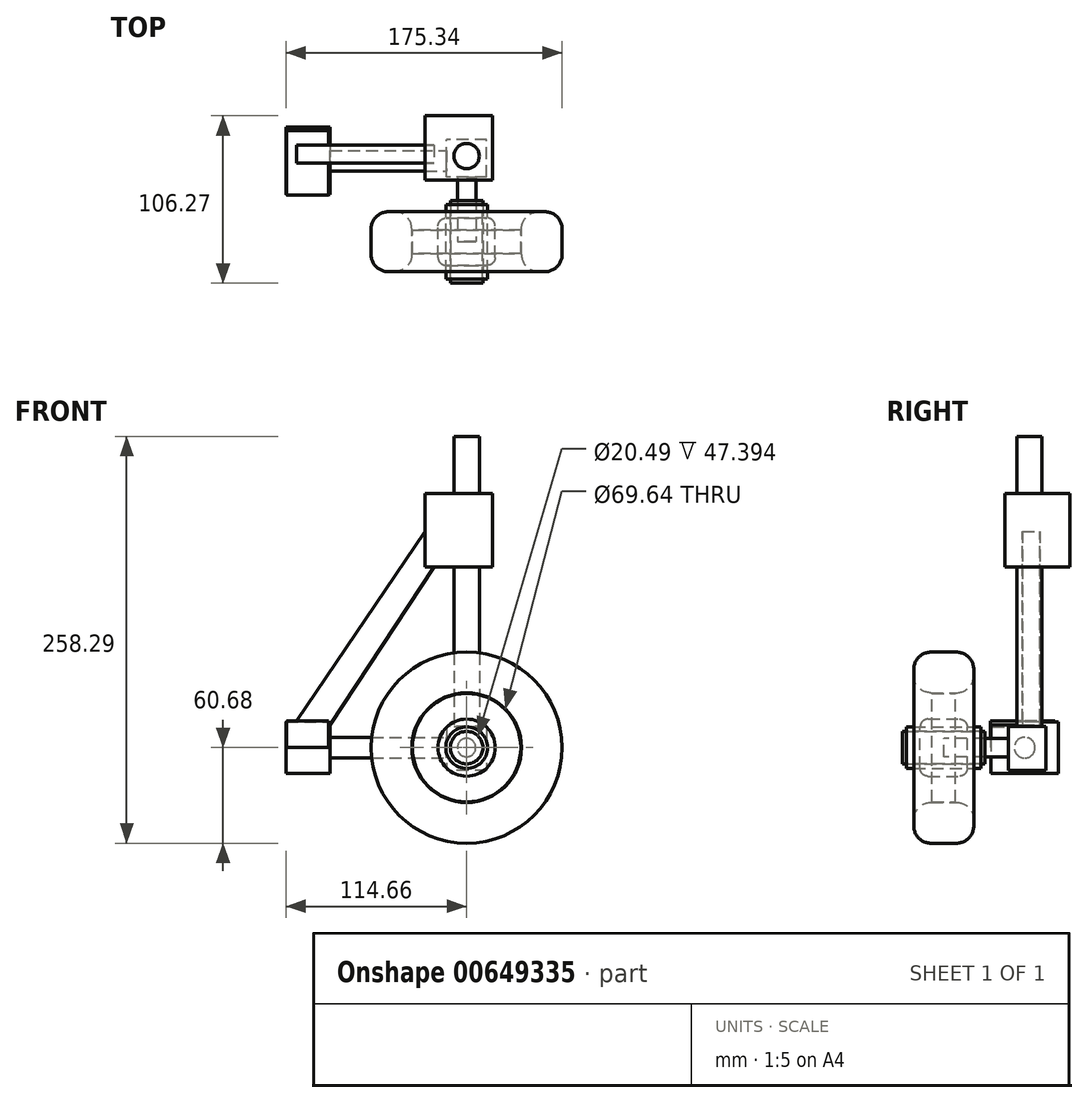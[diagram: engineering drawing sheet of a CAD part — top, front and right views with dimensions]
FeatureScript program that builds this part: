
annotation { "Feature Type Name" : "Feature", "Feature Type Description" : "" }
export const myFeature = defineFeature(function(context is Context, id is Id, definition is map)
    precondition{}
    {
        {
            var Q0;
            Q0=qCreatedBy(makeId("Front.planeOp"),FACE);
            var sketch = newSketch(context, id + "F0", { "sketchPlane" : qUnion([Q0])});
            skCircle(sketch, "E0", {"center": v(0, 0) * mm, "radius": 34.82 * mm});
            skCircle(sketch, "E1", {"center": v(0, 0) * mm, "radius": 60.68 * mm});
            skSolve(sketch);
        }
        {
            var Q0;
            Q0=makeQuery(id+"F0.imprint","IMPRINT",FACE,{"disambiguationData":[TD([[makeQuery(id+"F0.imprint","IMPRINT",EDGE,{"derivedFrom":sQuery(id+"F0.wireOp",EDGE,"E0")}),-1.0]])]});
            extrude(context, id + "F1", {"entities" : qUnion([Q0]), "endBound" : BoundingType.SYMMETRIC, "depth" : 38.1 * mm, "offsetDistance" : 25.4 * mm});
        }
        {
            var Q0;
            Q0=qCreatedBy(makeId("Front.planeOp"),FACE);
            var sketch = newSketch(context, id + "F2", { "sketchPlane" : qUnion([Q0])});
            skCircle(sketch, "E2", {"center": v(0, 0) * mm, "radius": 34.45 * mm});
            skSolve(sketch);
        }
        {
            var Q0;
            Q0 = qSketchRegion(id + "F2", true);
            extrude(context, id + "F3", {"entities" : qUnion([Q0]), "endBound" : BoundingType.SYMMETRIC, "depth" : 14.73 * mm, "offsetDistance" : 25.4 * mm});
        }
        {
            var Q0;
            Q0=makeQuery(id+"F1.opExtrude","CAP_EDGE",EDGE,{"disambiguationData":[OSD([sQuery(id+"F0.wireOp",EDGE,"E1")])],"isStart":true});
            var Q1;
            Q1=makeQuery(id+"F1.opExtrude","CAP_EDGE",EDGE,{"disambiguationData":[OSD([sQuery(id+"F0.wireOp",EDGE,"E0")])],"isStart":true});
            var Q2;
            Q2=makeQuery(id+"F1.opExtrude","CAP_EDGE",EDGE,{"disambiguationData":[OSD([sQuery(id+"F0.wireOp",EDGE,"E1")])],"isStart":false});
            var Q3;
            Q3=makeQuery(id+"F1.opExtrude","CAP_EDGE",EDGE,{"disambiguationData":[OSD([sQuery(id+"F0.wireOp",EDGE,"E0")])],"isStart":false});
            fillet(context, id + "F4", {"entities" : qUnion([Q0, Q1, Q2, Q3]), "radius" : 11.04 * mm, "tangentPropagation" : true, "allowEdgeOverflow" : false});
        }
        {
            var Q0;
            Q0=qCreatedBy(makeId("Front.planeOp"),FACE);
            var sketch = newSketch(context, id + "F5", { "sketchPlane" : qUnion([Q0])});
            skCircle(sketch, "E3", {"center": v(0, 0) * mm, "radius": 18.16 * mm});
            skSolve(sketch);
        }
        {
            var Q0;
            Q0 = qSketchRegion(id + "F5", true);
            extrude(context, id + "F6", {"entities" : qUnion([Q0]), "endBound" : BoundingType.SYMMETRIC, "depth" : 29.97 * mm, "offsetDistance" : 25.4 * mm});
        }
        {
            var Q0;
            Q0=makeQuery(id+"F6.opExtrude","CAP_EDGE",EDGE,{"disambiguationData":[OSD([sQuery(id+"F5.wireOp",EDGE,"E3")])],"isStart":false});
            var Q1;
            Q1=makeQuery(id+"F6.opExtrude","CAP_FACE",FACE,{"disambiguationData":[OSD([sQuery(id+"F5.wireOp",EDGE,"E3")])],"isStart":true});
            fillet(context, id + "F7", {"entities" : qUnion([Q0, Q1]), "radius" : 5.08 * mm, "tangentPropagation" : true, "allowEdgeOverflow" : false});
        }
        {
            var Q0;
            Q0=qCreatedBy(makeId("Front.planeOp"),FACE);
            var sketch = newSketch(context, id + "F8", { "sketchPlane" : qUnion([Q0])});
            skCircle(sketch, "E4", {"center": v(0, 0) * mm, "radius": 13.2 * mm});
            skCircle(sketch, "E5", {"center": v(0, 0) * mm, "radius": 10.25 * mm});
            skSolve(sketch);
        }
        {
            var Q0;
            Q0 = qSketchRegion(id + "F8", true);
            extrude(context, id + "F9", {"entities" : qUnion([Q0]), "endBound" : BoundingType.SYMMETRIC, "depth" : 47.4 * mm, "offsetDistance" : 25.4 * mm});
        }
        {
            var Q0;
            Q0=qCreatedBy(makeId("Front.planeOp"),FACE);
            var sketch = newSketch(context, id + "F10", { "sketchPlane" : qUnion([Q0])});
            skCircle(sketch, "E6", {"center": v(0, 0) * mm, "radius": 10.34 * mm});
            skSolve(sketch);
        }
        {
            var Q0;
            Q0 = qSketchRegion(id + "F10", true);
            extrude(context, id + "F11", {"entities" : qUnion([Q0]), "endBound" : BoundingType.SYMMETRIC, "oppositeDirection" : true, "depth" : 52.48 * mm, "offsetDistance" : 25.4 * mm});
        }
        {
            var Q0;
            Q0=qCreatedBy(makeId("Front.planeOp"),FACE);
            var sketch = newSketch(context, id + "F12", { "sketchPlane" : qUnion([Q0])});
            skCircle(sketch, "E7", {"center": v(0, 0) * mm, "radius": 5.84 * mm});
            skSolve(sketch);
        }
        {
            var Q0;
            Q0 = qSketchRegion(id + "F12", true);
            extrude(context, id + "F13", {"entities" : qUnion([Q0]), "oppositeDirection" : true, "depth" : 50.72 * mm, "offsetDistance" : 25.4 * mm});
        }
        {
            var Q0;
            Q0=qCreatedBy(makeId("Right.planeOp"),FACE);
            var sketch = newSketch(context, id + "F14", { "sketchPlane" : qUnion([Q0])});
            skLineSegment(sketch, "E8.bottom", {"start": v(41.05, 13.44) * mm, "end": v(64.93, 13.44) * mm});
            skLineSegment(sketch, "E8.top", {"start": v(41.05, -14.38) * mm, "end": v(64.93, -14.38) * mm});
            skLineSegment(sketch, "E8.left", {"start": v(41.05, 13.44) * mm, "end": v(41.05, -14.38) * mm});
            skLineSegment(sketch, "E8.right", {"start": v(64.93, 13.44) * mm, "end": v(64.93, -14.38) * mm});
            skSolve(sketch);
        }
        {
            var Q0;
            Q0 = qSketchRegion(id + "F14", true);
            extrude(context, id + "F15", {"entities" : qUnion([Q0]), "operationType" : NewBodyOperationType.ADD, "endBound" : BoundingType.SYMMETRIC, "depth" : 25.4 * mm, "offsetDistance" : 25.4 * mm});
        }
        {
            var Q0;
            Q0=qCreatedBy(makeId("Top.planeOp"),FACE);
            var sketch = newSketch(context, id + "F16", { "sketchPlane" : qUnion([Q0])});
            skCircle(sketch, "E9", {"center": v(0, 54.42) * mm, "radius": 8.07 * mm});
            skSolve(sketch);
        }
        {
            var Q0;
            Q0 = qSketchRegion(id + "F16", true);
            extrude(context, id + "F17", {"entities" : qUnion([Q0]), "operationType" : NewBodyOperationType.ADD, "depth" : 197.61 * mm, "offsetDistance" : 25.4 * mm});
        }
        {
            var Q0;
            Q0=qCreatedBy(makeId("Right.planeOp"),FACE);
            var sketch = newSketch(context, id + "F18", { "sketchPlane" : qUnion([Q0])});
            skCircle(sketch, "E10", {"center": v(51.45, 0) * mm, "radius": 6.59 * mm});
            skSolve(sketch);
        }
        {
            var Q0;
            Q0 = qSketchRegion(id + "F18", true);
            extrude(context, id + "F19", {"entities" : qUnion([Q0]), "operationType" : NewBodyOperationType.ADD, "oppositeDirection" : true, "depth" : 106.85 * mm, "offsetDistance" : 25.4 * mm});
        }
        {
            var Q0;
            Q0=qCreatedBy(makeId("Front.planeOp"),FACE);
            var sketch = newSketch(context, id + "F20", { "sketchPlane" : qUnion([Q0])});
            skLineSegment(sketch, "E11.bottom", {"start": v(-86.73, 16.5) * mm, "end": v(-114.66, 16.5) * mm});
            skLineSegment(sketch, "E11.top", {"start": v(-86.73, -16.5) * mm, "end": v(-114.66, -16.5) * mm});
            skLineSegment(sketch, "E11.left", {"start": v(-86.73, 16.5) * mm, "end": v(-86.73, -16.5) * mm});
            skLineSegment(sketch, "E11.right", {"start": v(-114.66, 16.5) * mm, "end": v(-114.66, -16.5) * mm});
            skPoint(sketch, "E11.middle", {"position": v(-100.7, 0) * mm});
            skSolve(sketch);
        }
        {
            var Q0;
            Q0=makeQuery(id+"F20.imprint","IMPRINT",FACE,{"disambiguationData":[TD([[makeQuery(id+"F20.imprint","IMPRINT",EDGE,{"derivedFrom":sQuery(id+"F20.wireOp",EDGE,"E11.bottom")}),1.0]])]});
            extrude(context, id + "F21", {"entities" : qUnion([Q0]), "operationType" : NewBodyOperationType.ADD, "oppositeDirection" : true, "depth" : 72.76 * mm, "offsetDistance" : 25.4 * mm});
        }
        {
            var Q0;
            Q0=makeQuery(id+"F21.opExtrude","CAP_FACE",FACE,{"disambiguationData":[OSD([sQuery(id+"F20.wireOp",EDGE,"E11.bottom"),sQuery(id+"F20.wireOp",EDGE,"E11.top"),sQuery(id+"F20.wireOp",EDGE,"E11.left"),sQuery(id+"F20.wireOp",EDGE,"E11.right")])],"isStart":true});
            extrude(context, id + "F22", {"entities" : qUnion([Q0]), "operationType" : NewBodyOperationType.REMOVE, "oppositeDirection" : true, "depth" : 30.1 * mm, "offsetDistance" : 25.4 * mm});
        }
        {
            var Q0;
            Q0=qCreatedBy(makeId("Front.planeOp"),FACE);
            var sketch = newSketch(context, id + "F23", { "sketchPlane" : qUnion([Q0])});
            skLineSegment(sketch, "E12", {"start": v(-109.7, 14.62) * mm, "end": v(-13.9, 155.72) * mm});
            skLineSegment(sketch, "E13", {"start": v(-13.9, 155.72) * mm, "end": v(0, 146.29) * mm});
            skLineSegment(sketch, "E14", {"start": v(0, 146.29) * mm, "end": v(-96.22, 0) * mm});
            skLineSegment(sketch, "E15", {"start": v(-96.22, 0) * mm, "end": v(-109.7, 14.62) * mm});
            skSolve(sketch);
        }
        {
            var Q0;
            Q0=makeQuery(id+"F23.imprint","IMPRINT",FACE,{"disambiguationData":[TD([[makeQuery(id+"F23.imprint","IMPRINT",EDGE,{"derivedFrom":sQuery(id+"F23.wireOp",EDGE,"E12")}),-1.0]])]});
            extrude(context, id + "F24", {"entities" : qUnion([Q0]), "operationType" : NewBodyOperationType.ADD, "oppositeDirection" : true, "depth" : 61.23 * mm, "offsetDistance" : 25.4 * mm});
        }
        {
            var Q0;
            Q0=makeQuery(id+"F24.opExtrude","CAP_FACE",FACE,{"disambiguationData":[OSD([sQuery(id+"F23.wireOp",EDGE,"E12"),sQuery(id+"F23.wireOp",EDGE,"E13"),sQuery(id+"F23.wireOp",EDGE,"E14"),sQuery(id+"F23.wireOp",EDGE,"E15")])],"isStart":true});
            extrude(context, id + "F25", {"entities" : qUnion([Q0]), "operationType" : NewBodyOperationType.REMOVE, "oppositeDirection" : true, "depth" : 50.06 * mm, "offsetDistance" : 25.4 * mm});
        }
        {
            var Q0;
            Q0=qCreatedBy(makeId("Front.planeOp"),FACE);
            var sketch = newSketch(context, id + "F26", { "sketchPlane" : qUnion([Q0])});
            skLineSegment(sketch, "E16.bottom", {"start": v(-26.38, 161.4) * mm, "end": v(16.55, 161.4) * mm});
            skLineSegment(sketch, "E16.top", {"start": v(-26.38, 114.78) * mm, "end": v(16.55, 114.78) * mm});
            skLineSegment(sketch, "E16.left", {"start": v(-26.38, 161.4) * mm, "end": v(-26.38, 114.78) * mm});
            skLineSegment(sketch, "E16.right", {"start": v(16.55, 161.4) * mm, "end": v(16.55, 114.78) * mm});
            skSolve(sketch);
        }
        {
            var Q0;
            Q0=makeQuery(id+"F26.imprint","IMPRINT",FACE,{"disambiguationData":[TD([[makeQuery(id+"F26.imprint","IMPRINT",EDGE,{"derivedFrom":sQuery(id+"F26.wireOp",EDGE,"E16.bottom")}),-1.0]])]});
            extrude(context, id + "F27", {"entities" : qUnion([Q0]), "operationType" : NewBodyOperationType.ADD, "oppositeDirection" : true, "depth" : 80.03 * mm, "offsetDistance" : 25.4 * mm});
        }
        {
            var Q0;
            Q0=makeQuery(id+"F27.opExtrude","CAP_FACE",FACE,{"disambiguationData":[OSD([sQuery(id+"F26.wireOp",EDGE,"E16.bottom"),sQuery(id+"F26.wireOp",EDGE,"E16.top"),sQuery(id+"F26.wireOp",EDGE,"E16.left"),sQuery(id+"F26.wireOp",EDGE,"E16.right")])],"isStart":true});
            extrude(context, id + "F28", {"entities" : qUnion([Q0]), "operationType" : NewBodyOperationType.REMOVE, "oppositeDirection" : true, "depth" : 39 * mm, "offsetDistance" : 25.4 * mm});
        }
        {
            var Q0;
            Q0=qCreatedBy(makeId("Front.planeOp"),FACE);
            var sketch = newSketch(context, id + "F29", { "sketchPlane" : qUnion([Q0])});
            skLineSegment(sketch, "E17.bottom", {"start": v(-114.51, 17.12) * mm, "end": v(-87.73, 17.12) * mm});
            skLineSegment(sketch, "E17.top", {"start": v(-114.51, 0) * mm, "end": v(-87.73, 0) * mm});
            skLineSegment(sketch, "E17.left", {"start": v(-114.51, 17.12) * mm, "end": v(-114.51, 0) * mm});
            skLineSegment(sketch, "E17.right", {"start": v(-87.73, 17.12) * mm, "end": v(-87.73, 0) * mm});
            skSolve(sketch);
        }
        {
            var Q0;
            Q0 = qSketchRegion(id + "F29", true);
            extrude(context, id + "F30", {"entities" : qUnion([Q0]), "operationType" : NewBodyOperationType.ADD, "oppositeDirection" : true, "depth" : 70.73 * mm, "offsetDistance" : 25.4 * mm});
        }
        {
            var Q0;
            Q0=makeQuery(id+"F30.opExtrude","CAP_FACE",FACE,{"disambiguationData":[OSD([sQuery(id+"F29.wireOp",EDGE,"E17.bottom"),sQuery(id+"F29.wireOp",EDGE,"E17.top"),sQuery(id+"F29.wireOp",EDGE,"E17.left"),sQuery(id+"F29.wireOp",EDGE,"E17.right")])],"isStart":true});
            extrude(context, id + "F31", {"entities" : qUnion([Q0]), "operationType" : NewBodyOperationType.REMOVE, "oppositeDirection" : true, "depth" : 29.79 * mm, "offsetDistance" : 25.4 * mm});
        }
    });
